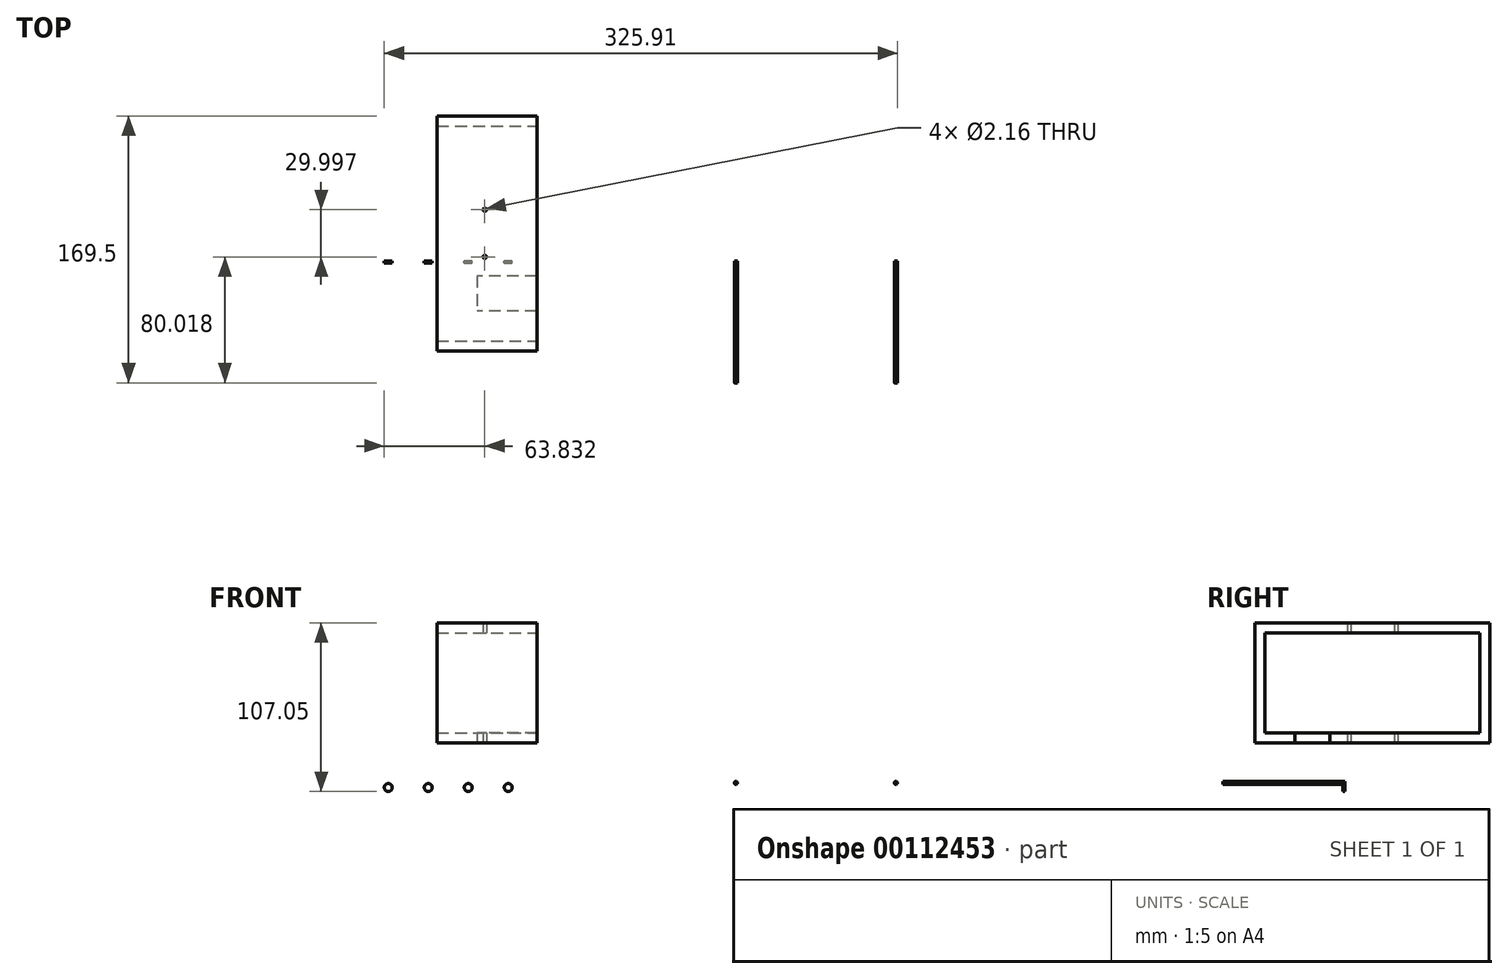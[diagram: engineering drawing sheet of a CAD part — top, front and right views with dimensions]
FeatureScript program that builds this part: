
annotation { "Feature Type Name" : "Feature", "Feature Type Description" : "" }
export const myFeature = defineFeature(function(context is Context, id is Id, definition is map)
    precondition{}
    {
        {
            var Q0;
            Q0=qCreatedBy(makeId("Top.planeOp"),FACE);
            var sketch = newSketch(context, id + "F0", { "sketchPlane" : qUnion([Q0])});
            skLineSegment(sketch, "E0.bottom", {"start": v(-30.98, 92.03) * mm, "end": v(32.52, 92.03) * mm});
            skLineSegment(sketch, "E0.top", {"start": v(-30.98, -57.2) * mm, "end": v(32.52, -57.2) * mm});
            skLineSegment(sketch, "E0.left", {"start": v(-30.98, 92.03) * mm, "end": v(-30.98, -57.2) * mm});
            skLineSegment(sketch, "E1.bottom", {"start": v(32.52, -9.57) * mm, "end": v(-5.58, -9.57) * mm});
            skLineSegment(sketch, "E1.top", {"start": v(32.52, -31.8) * mm, "end": v(-5.58, -31.8) * mm});
            skLineSegment(sketch, "E1.right", {"start": v(-5.58, -9.57) * mm, "end": v(-5.58, -31.8) * mm});
            skLineSegment(sketch, "E2", {"start": v(32.52, 92.03) * mm, "end": v(32.52, -9.57) * mm});
            skLineSegment(sketch, "E3", {"start": v(32.52, -31.8) * mm, "end": v(32.52, -57.2) * mm});
            skLineSegment(sketch, "E4", {"start": v(32.52, -9.57) * mm, "end": v(32.52, -31.8) * mm});
            skSolve(sketch);
        }
        {
            var Q0;
            Q0=makeQuery(id+"F0.imprint","IMPRINT",FACE,{"disambiguationData":[TD([[makeQuery(id+"F0.imprint","IMPRINT",EDGE,{"derivedFrom":sQuery(id+"F0.wireOp",EDGE,"E0.bottom")}),-1.0]])]});
            extrude(context, id + "F1", {"entities" : qUnion([Q0]), "depth" : 6.35 * mm});
        }
        {
            var Q0;
            Q0=makeQuery(id+"F1.opExtrude","CAP_FACE",FACE,{"disambiguationData":[OSD([sQuery(id+"F0.wireOp",EDGE,"E0.bottom"),sQuery(id+"F0.wireOp",EDGE,"E0.top"),sQuery(id+"F0.wireOp",EDGE,"E0.left"),sQuery(id+"F0.wireOp",EDGE,"E0.right"),sQuery(id+"F0.wireOp",EDGE,"C7GEYsDE-jDmz-jZbS-rBoS-36cmIwXAHciw.bottom"),sQuery(id+"F0.wireOp",EDGE,"C7GEYsDE-jDmz-jZbS-rBoS-36cmIwXAHciw.top"),sQuery(id+"F0.wireOp",EDGE,"C7GEYsDE-jDmz-jZbS-rBoS-36cmIwXAHciw.right"),sQuery(id+"F0.wireOp",EDGE,"154f1382-312a-4bea-8aee-66d54dca946d.trimOffspring")])],"isStart":false});
            var sketch = newSketch(context, id + "F2", { "sketchPlane" : qUnion([Q0])});
            skLineSegment(sketch, "E5.bottom", {"start": v(-30.98, 92.03) * mm, "end": v(-30.98, 92.03) * mm});
            skLineSegment(sketch, "E5.top", {"start": v(-30.98, 85.68) * mm, "end": v(-30.98, 85.68) * mm});
            skLineSegment(sketch, "E5.left", {"start": v(-30.98, 92.03) * mm, "end": v(-30.98, 85.68) * mm});
            skLineSegment(sketch, "E5.right", {"start": v(-30.98, 92.03) * mm, "end": v(-30.98, 85.68) * mm});
            skLineSegment(sketch, "E6.bottom", {"start": v(-30.98, -57.2) * mm, "end": v(-30.98, -57.2) * mm});
            skLineSegment(sketch, "E6.top", {"start": v(-30.98, -50.84) * mm, "end": v(-30.98, -50.84) * mm});
            skLineSegment(sketch, "E6.left", {"start": v(-30.98, -57.2) * mm, "end": v(-30.98, -50.84) * mm});
            skLineSegment(sketch, "E6.right", {"start": v(-30.98, -57.2) * mm, "end": v(-30.98, -50.84) * mm});
            skLineSegment(sketch, "E7.left", {"start": v(-30.98, -50.84) * mm, "end": v(-30.98, -57.2) * mm});
            skLineSegment(sketch, "E8.bottom", {"start": v(-30.98, -50.84) * mm, "end": v(32.52, -50.84) * mm});
            skLineSegment(sketch, "E8.top", {"start": v(-30.98, -57.2) * mm, "end": v(32.52, -57.2) * mm});
            skLineSegment(sketch, "E8.right", {"start": v(32.52, -50.84) * mm, "end": v(32.52, -57.2) * mm});
            skLineSegment(sketch, "E9.bottom", {"start": v(-30.98, 85.68) * mm, "end": v(32.52, 85.68) * mm});
            skLineSegment(sketch, "E9.top", {"start": v(-30.98, 92.03) * mm, "end": v(32.52, 92.03) * mm});
            skLineSegment(sketch, "E9.left", {"start": v(-30.98, 85.68) * mm, "end": v(-30.98, 92.03) * mm});
            skLineSegment(sketch, "E9.right", {"start": v(32.52, 85.68) * mm, "end": v(32.52, 92.03) * mm});
            skSolve(sketch);
        }
        {
            var Q0;
            Q0 = qSketchRegion(id + "F2", true);
            extrude(context, id + "F3", {"entities" : qUnion([Q0]), "operationType" : NewBodyOperationType.ADD, "depth" : 31.75 * mm});
        }
        {
            var Q0;
            Q0=makeQuery(id+"F1.opExtrude","SWEPT_BODY",BODY,{"disambiguationData":[OSD([sQuery(id+"F0.wireOp",EDGE,"E0.bottom"),sQuery(id+"F0.wireOp",EDGE,"E0.top"),sQuery(id+"F0.wireOp",EDGE,"E0.left"),sQuery(id+"F0.wireOp",EDGE,"E1.bottom"),sQuery(id+"F0.wireOp",EDGE,"E1.top"),sQuery(id+"F0.wireOp",EDGE,"E1.right"),sQuery(id+"F0.wireOp",EDGE,"E2"),sQuery(id+"F0.wireOp",EDGE,"E3")])]});
            var Q1;
            Q1=makeQuery(id+"F3.opExtrude","CAP_FACE",FACE,{"disambiguationData":[OSD([sQuery(id+"F2.wireOp",EDGE,"E8.bottom"),sQuery(id+"F2.wireOp",EDGE,"E8.top"),sQuery(id+"F2.wireOp",EDGE,"E7.left"),sQuery(id+"F2.wireOp",EDGE,"E8.right")])],"isStart":false});
            mirror(context, id + "F4", {"operationType" : NewBodyOperationType.ADD, "entities" : qUnion([Q0]), "mirrorPlane" : qUnion([Q1])});
        }
        {
            var Q0;
            Q0=makeQuery(id+"F4.opPattern","COPY",FACE,{"derivedFrom":makeQuery(id+"F1.opExtrude","CAP_FACE",FACE,{"disambiguationData":[OSD([sQuery(id+"F0.wireOp",EDGE,"E0.bottom"),sQuery(id+"F0.wireOp",EDGE,"E0.top"),sQuery(id+"F0.wireOp",EDGE,"E0.left"),sQuery(id+"F0.wireOp",EDGE,"E1.bottom"),sQuery(id+"F0.wireOp",EDGE,"E1.top"),sQuery(id+"F0.wireOp",EDGE,"E1.right"),sQuery(id+"F0.wireOp",EDGE,"E2"),sQuery(id+"F0.wireOp",EDGE,"E3")])],"isStart":true}),"instanceName":"1"});
            var sketch = newSketch(context, id + "F5", { "sketchPlane" : qUnion([Q0])});
            skLineSegment(sketch, "E10", {"start": v(32.52, -31.8) * mm, "end": v(32.52, -9.57) * mm});
            skSolve(sketch);
        }
        {
            var Q0;
            Q0=makeQuery(id+"F5.imprint","IMPRINT",FACE,{"disambiguationData":[TD([[makeQuery(id+"F5.imprint","IMPRINT",EDGE,{"derivedFrom":sQuery(id+"F5.wireOp",EDGE,"E10")}),1.0]])]});
            extrude(context, id + "F6", {"entities" : qUnion([Q0]), "operationType" : NewBodyOperationType.ADD, "oppositeDirection" : true, "depth" : 6.35 * mm});
        }
        {
            var Q0;
            Q0=makeQuery(id+"F1.opExtrude","CAP_FACE",FACE,{"disambiguationData":[OSD([sQuery(id+"F0.wireOp",EDGE,"E0.bottom"),sQuery(id+"F0.wireOp",EDGE,"E0.top"),sQuery(id+"F0.wireOp",EDGE,"E0.left"),sQuery(id+"F0.wireOp",EDGE,"E1.bottom"),sQuery(id+"F0.wireOp",EDGE,"E1.top"),sQuery(id+"F0.wireOp",EDGE,"E1.right"),sQuery(id+"F0.wireOp",EDGE,"E2"),sQuery(id+"F0.wireOp",EDGE,"E3")])],"isStart":true});
            var sketch = newSketch(context, id + "F7", { "sketchPlane" : qUnion([Q0])});
            skLineSegment(sketch, "E11.bottom", {"start": v(-5.58, 9.57) * mm, "end": v(-0.58, 9.57) * mm});
            skLineSegment(sketch, "E11.top", {"start": v(-5.58, -2.55) * mm, "end": v(-0.58, -2.55) * mm});
            skLineSegment(sketch, "E11.left", {"start": v(-5.58, 9.57) * mm, "end": v(-5.58, -2.55) * mm});
            skLineSegment(sketch, "E11.right", {"start": v(-0.58, 9.57) * mm, "end": v(-0.58, -2.55) * mm});
            skCircle(sketch, "E12", {"center": v(-0.58, -2.55) * mm, "radius": 1.08 * mm});
            skCircle(sketch, "E13", {"center": v(-0.58, -32.55) * mm, "radius": 1.08 * mm});
            skSolve(sketch);
        }
        {
            var Q0;
            {var subQ0=sQuery(id+"F7.wireOp",EDGE,"E11.right");var subQ1=sQuery(id+"F7.wireOp",EDGE,"E11.top");var subQ2=makeQuery(id+"F7.imprint","INTERSECT",VERTEX,{"derivedFrom":[subQ1,subQ0]});Q0=makeQuery(id+"F7.imprint","IMPRINT",FACE,{"disambiguationData":[TD([[makeQuery(id+"F7.imprint","IMPRINT",EDGE,{"disambiguationData":[TD([[subQ2,1.0]])],"derivedFrom":subQ1}),-1.0]])]});}
            var Q1;
            {var subQ0=sQuery(id+"F7.wireOp",EDGE,"E11.right");var subQ1=sQuery(id+"F7.wireOp",EDGE,"E11.top");var subQ2=makeQuery(id+"F7.imprint","INTERSECT",VERTEX,{"derivedFrom":[subQ1,subQ0]});Q1=makeQuery(id+"F7.imprint","IMPRINT",FACE,{"disambiguationData":[TD([[makeQuery(id+"F7.imprint","IMPRINT",EDGE,{"disambiguationData":[TD([[subQ2,1.0]])],"derivedFrom":subQ1}),1.0]])]});}
            extrude(context, id + "F8", {"entities" : qUnion([Q0, Q1]), "operationType" : NewBodyOperationType.REMOVE, "oppositeDirection" : true, "depth" : 508 * mm});
        }
        {
            var Q0;
            Q0=qCreatedBy(makeId("Front.planeOp"),FACE);
            var sketch = newSketch(context, id + "F9", { "sketchPlane" : qUnion([Q0])});
            skCircle(sketch, "E14", {"center": v(-61.87, -28.31) * mm, "radius": 2.54 * mm});
            skSolve(sketch);
        }
        {
            var Q0;
            Q0=makeQuery(id+"F9.imprint","IMPRINT",FACE,{"disambiguationData":[TD([[makeQuery(id+"F9.imprint","IMPRINT",EDGE,{"derivedFrom":sQuery(id+"F9.wireOp",EDGE,"E14")}),1.0]])]});
            extrude(context, id + "F10", {"entities" : qUnion([Q0]), "depth" : 1.27 * mm});
        }
        {
            var Q0;
            Q0=makeQuery(id+"F10.opExtrude","SWEPT_BODY",BODY,{"disambiguationData":[OSD([sQuery(id+"F9.wireOp",EDGE,"E14")])]});
            transform(context, id + "F11", {"entities" : qUnion([Q0]), "transformType" : TransformType.TRANSLATION_3D, "dx" : 76.2 * mm, "dy" : 0 * mm, "dz" : 0 * mm, "makeCopy" : true});
        }
        {
            var Q0;
            Q0=makeQuery(id+"F10.opExtrude","SWEPT_BODY",BODY,{"disambiguationData":[OSD([sQuery(id+"F9.wireOp",EDGE,"E14")])]});
            transform(context, id + "F12", {"entities" : qUnion([Q0]), "transformType" : TransformType.TRANSLATION_3D, "dx" : 25.4 * mm, "dy" : 0 * mm, "dz" : 0 * mm, "makeCopy" : true});
        }
        {
            var Q0;
            Q0=makeQuery(id+"F10.opExtrude","SWEPT_BODY",BODY,{"disambiguationData":[OSD([sQuery(id+"F9.wireOp",EDGE,"E14")])]});
            transform(context, id + "F13", {"entities" : qUnion([Q0]), "transformType" : TransformType.TRANSLATION_3D, "dx" : 50.8 * mm, "dy" : 0 * mm, "dz" : 0 * mm, "makeCopy" : true});
        }
        {
            var Q0;
            Q0=qCreatedBy(makeId("Front.planeOp"),FACE);
            var sketch = newSketch(context, id + "F14", { "sketchPlane" : qUnion([Q0])});
            skCircle(sketch, "E15", {"center": v(158.9, -25.4) * mm, "radius": 1 * mm});
            skSolve(sketch);
        }
        {
            var Q0;
            Q0 = qSketchRegion(id + "F14", true);
            extrude(context, id + "F15", {"entities" : qUnion([Q0]), "depth" : 77.47 * mm});
        }
        {
            var Q0;
            Q0=makeQuery(id+"F15.opExtrude","SWEPT_BODY",BODY,{"disambiguationData":[OSD([sQuery(id+"F14.wireOp",EDGE,"E15")])]});
            transform(context, id + "F16", {"entities" : qUnion([Q0]), "transformType" : TransformType.TRANSLATION_3D, "dx" : 101.6 * mm, "dy" : 0 * mm, "dz" : 0 * mm, "makeCopy" : true});
        }
        {
            var Q0;
            Q0=makeQuery(id+"F7.imprint","IMPRINT",FACE,{"disambiguationData":[TD([[makeQuery(id+"F7.imprint","IMPRINT",EDGE,{"derivedFrom":sQuery(id+"F7.wireOp",EDGE,"E13")}),1.0]])]});
            extrude(context, id + "F17", {"entities" : qUnion([Q0]), "operationType" : NewBodyOperationType.REMOVE, "oppositeDirection" : true, "depth" : 508 * mm});
        }
    });
